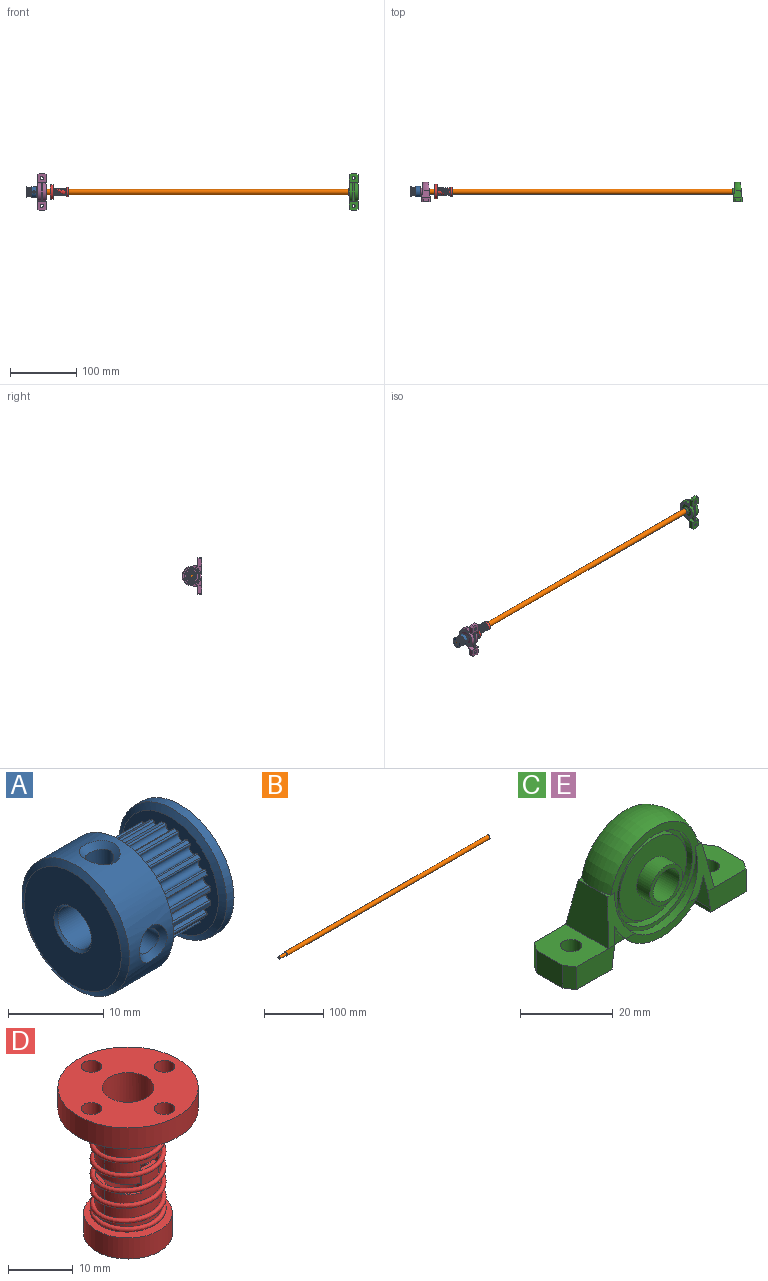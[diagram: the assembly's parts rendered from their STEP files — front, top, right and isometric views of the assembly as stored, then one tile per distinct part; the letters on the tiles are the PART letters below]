
ASSEMBLY  parts=5 mates=5
PART A: 99 faces, bbox 16x16.1x16.3 mm
  f0: plane 16.3x16.15mm, normal (1,0,0), area 136.4mm2, adj f1,f2
  f1: cylinder r=8mm len=16mm, axis (-1,0,0), area 55.3mm2, adj f0,f3
  f2: cone r=4.38mm half-angle=45deg, axis (1,0,0), area 6mm2, adj f0,f4
  f3: cone r=7.21mm half-angle=60.2deg, axis (1,0,0), area 43.3mm2, adj f1,f5
  f4: cone r=4.23mm half-angle=45deg, axis (-1,0,0), area 5.8mm2, adj f2,f6
  f5: plane 14.69x14.43mm, normal (-1,0,0), area 61.1mm2, adj f3,f7,f8,f9,f10,f11,f12,f13
  f6: plane 8.62x8.54mm, normal (1,0,0), area 31.6mm2, adj f4,f87
  f7: cylinder r=0.55mm len=7mm, axis (-1,0,0), area 12.5mm2, adj f5,f8,f86,f90
  f8: cylinder r=0.16mm len=7mm, axis (-1,0,0), area 2mm2, adj f5,f7,f9,f90
  f9: cylinder r=6.11mm len=7mm, axis (-1,0,0), area 3.2mm2, adj f5,f8,f10,f90
  f10: cylinder r=0.16mm len=7mm, axis (1,0,0), area 2mm2, adj f5,f9,f11,f90
  f11: cylinder r=0.55mm len=7mm, axis (-1,0,0), area 12.5mm2, adj f5,f10,f12,f90
  f12: cylinder r=0.16mm len=7mm, axis (-1,0,0), area 2mm2, adj f5,f11,f13,f90
  f13: cylinder r=6.11mm len=7mm, axis (-1,0,0), area 3.2mm2, adj f5,f12,f14,f90
  f14: cylinder r=0.16mm len=7mm, axis (1,0,0), area 2mm2, adj f5,f13,f15,f90
  f15: cylinder r=0.55mm len=7mm, axis (-1,0,0), area 12.5mm2, adj f5,f14,f16,f90
  f16: cylinder r=0.16mm len=7mm, axis (-1,0,0), area 2mm2, adj f5,f15,f17,f90
  f17: cylinder r=6.11mm len=7mm, axis (-1,0,0), area 3.2mm2, adj f5,f16,f18,f90
  f18: cylinder r=0.16mm len=7mm, axis (1,0,0), area 2mm2, adj f5,f17,f19,f90
  f19: cylinder r=0.55mm len=7mm, axis (-1,0,0), area 12.5mm2, adj f5,f18,f20,f90
  f20: cylinder r=0.16mm len=7mm, axis (-1,0,0), area 2mm2, adj f5,f19,f21,f90
  f21: cylinder r=6.11mm len=7mm, axis (-1,0,0), area 3.2mm2, adj f5,f20,f22,f90
  f22: cylinder r=0.16mm len=7mm, axis (1,0,0), area 2mm2, adj f5,f21,f23,f90
  f23: cylinder r=0.55mm len=7mm, axis (-1,0,0), area 12.5mm2, adj f5,f22,f24,f90
  f24: cylinder r=0.16mm len=7mm, axis (-1,0,0), area 2mm2, adj f5,f23,f25,f90
  f25: cylinder r=6.11mm len=7mm, axis (-1,0,0), area 3.2mm2, adj f5,f24,f26,f90
  f26: cylinder r=0.16mm len=7mm, axis (1,0,0), area 2mm2, adj f5,f25,f27,f90
  f27: cylinder r=0.55mm len=7mm, axis (-1,0,0), area 12.5mm2, adj f5,f26,f28,f90
  f28: cylinder r=0.16mm len=7mm, axis (-1,0,0), area 2mm2, adj f5,f27,f29,f90
  f29: cylinder r=6.11mm len=7mm, axis (-1,0,0), area 3.2mm2, adj f5,f28,f30,f90
  f30: cylinder r=0.16mm len=7mm, axis (1,0,0), area 2mm2, adj f5,f29,f31,f90
  f31: cylinder r=0.55mm len=7mm, axis (-1,0,0), area 12.5mm2, adj f5,f30,f32,f90
  f32: cylinder r=0.16mm len=7mm, axis (-1,0,0), area 2mm2, adj f5,f31,f33,f90
  f33: cylinder r=6.11mm len=7mm, axis (-1,0,0), area 3.2mm2, adj f5,f32,f34,f90
  f34: cylinder r=0.16mm len=7mm, axis (1,0,0), area 2mm2, adj f5,f33,f35,f90
  f35: cylinder r=0.55mm len=7mm, axis (-1,0,0), area 12.5mm2, adj f5,f34,f36,f90
  f36: cylinder r=0.16mm len=7mm, axis (-1,0,0), area 2mm2, adj f5,f35,f37,f90
  f37: cylinder r=6.11mm len=7mm, axis (-1,0,0), area 3.2mm2, adj f5,f36,f38,f90
  f38: cylinder r=0.16mm len=7mm, axis (1,0,0), area 2mm2, adj f5,f37,f39,f90
  f39: cylinder r=0.55mm len=7mm, axis (-1,0,0), area 12.5mm2, adj f5,f38,f40,f90
  f40: cylinder r=0.16mm len=7mm, axis (-1,0,0), area 2mm2, adj f5,f39,f41,f90
  f41: cylinder r=6.11mm len=7mm, axis (-1,0,0), area 3.2mm2, adj f5,f40,f42,f90
  f42: cylinder r=0.16mm len=7mm, axis (1,0,0), area 2mm2, adj f5,f41,f43,f90
  f43: cylinder r=0.55mm len=7mm, axis (-1,0,0), area 12.5mm2, adj f5,f42,f44,f90
  f44: cylinder r=0.16mm len=7mm, axis (-1,0,0), area 2mm2, adj f5,f43,f45,f90
  f45: cylinder r=6.11mm len=7mm, axis (-1,0,0), area 3.2mm2, adj f5,f44,f46,f90
  f46: cylinder r=0.16mm len=7mm, axis (1,0,0), area 2mm2, adj f5,f45,f47,f90
  f47: cylinder r=0.55mm len=7mm, axis (-1,0,0), area 12.5mm2, adj f5,f46,f48,f90
  f48: cylinder r=0.16mm len=7mm, axis (-1,0,0), area 2mm2, adj f5,f47,f49,f90
  f49: cylinder r=6.11mm len=7mm, axis (-1,0,0), area 3.2mm2, adj f5,f48,f50,f90
  f50: cylinder r=0.16mm len=7mm, axis (1,0,0), area 2mm2, adj f5,f49,f51,f90
  f51: cylinder r=0.55mm len=7mm, axis (-1,0,0), area 12.5mm2, adj f5,f50,f52,f90
  f52: cylinder r=0.16mm len=7mm, axis (-1,0,0), area 2mm2, adj f5,f51,f53,f90
  f53: cylinder r=6.11mm len=7mm, axis (-1,0,0), area 3.2mm2, adj f5,f52,f54,f90
  f54: cylinder r=0.16mm len=7mm, axis (1,0,0), area 2mm2, adj f5,f53,f55,f90
  f55: cylinder r=0.55mm len=7mm, axis (-1,0,0), area 12.5mm2, adj f5,f54,f56,f90
  f56: cylinder r=0.16mm len=7mm, axis (-1,0,0), area 2mm2, adj f5,f55,f57,f90
  f57: cylinder r=6.11mm len=7mm, axis (-1,0,0), area 3.2mm2, adj f5,f56,f58,f90
  f58: cylinder r=0.16mm len=7mm, axis (1,0,0), area 2mm2, adj f5,f57,f59,f90
  f59: cylinder r=0.55mm len=7mm, axis (-1,0,0), area 12.5mm2, adj f5,f58,f60,f90
  f60: cylinder r=0.16mm len=7mm, axis (-1,0,0), area 2mm2, adj f5,f59,f61,f90
  f61: cylinder r=6.11mm len=7mm, axis (-1,0,0), area 3.2mm2, adj f5,f60,f62,f90
  f62: cylinder r=0.16mm len=7mm, axis (1,0,0), area 2mm2, adj f5,f61,f63,f90
  f63: cylinder r=0.55mm len=7mm, axis (-1,0,0), area 12.5mm2, adj f5,f62,f64,f90
  f64: cylinder r=0.16mm len=7mm, axis (-1,0,0), area 2mm2, adj f5,f63,f65,f90
  f65: cylinder r=6.11mm len=7mm, axis (-1,0,0), area 3.2mm2, adj f5,f64,f66,f90
  f66: cylinder r=0.16mm len=7mm, axis (1,0,0), area 2mm2, adj f5,f65,f67,f90
  f67: cylinder r=0.55mm len=7mm, axis (-1,0,0), area 12.5mm2, adj f5,f66,f68,f90
  f68: cylinder r=0.16mm len=7mm, axis (-1,0,0), area 2mm2, adj f5,f67,f69,f90
  f69: cylinder r=6.11mm len=7mm, axis (-1,0,0), area 3.2mm2, adj f5,f68,f70,f90
  f70: cylinder r=0.16mm len=7mm, axis (1,0,0), area 2mm2, adj f5,f69,f71,f90
  f71: cylinder r=0.55mm len=7mm, axis (-1,0,0), area 12.5mm2, adj f5,f70,f72,f90
  f72: cylinder r=0.16mm len=7mm, axis (-1,0,0), area 2mm2, adj f5,f71,f73,f90
  f73: cylinder r=6.11mm len=7mm, axis (-1,0,0), area 3.2mm2, adj f5,f72,f74,f90
  f74: cylinder r=0.16mm len=7mm, axis (1,0,0), area 2mm2, adj f5,f73,f75,f90
  f75: cylinder r=0.55mm len=7mm, axis (-1,0,0), area 12.5mm2, adj f5,f74,f76,f90
  f76: cylinder r=0.16mm len=7mm, axis (-1,0,0), area 2mm2, adj f5,f75,f77,f90
  f77: cylinder r=6.11mm len=7mm, axis (-1,0,0), area 3.2mm2, adj f5,f76,f78,f90
  f78: cylinder r=0.16mm len=7mm, axis (1,0,0), area 2mm2, adj f5,f77,f79,f90
  f79: cylinder r=0.55mm len=7mm, axis (-1,0,0), area 12.5mm2, adj f5,f78,f80,f90
  f80: cylinder r=0.16mm len=7mm, axis (-1,0,0), area 2mm2, adj f5,f79,f81,f90
  f81: cylinder r=6.11mm len=7mm, axis (-1,0,0), area 3.2mm2, adj f5,f80,f82,f90
  f82: cylinder r=0.16mm len=7mm, axis (1,0,0), area 2mm2, adj f5,f81,f83,f90
  f83: cylinder r=0.55mm len=7mm, axis (-1,0,0), area 12.5mm2, adj f5,f82,f84,f90
  f84: cylinder r=0.16mm len=7mm, axis (-1,0,0), area 2mm2, adj f5,f83,f85,f90
  f85: cylinder r=6.11mm len=7mm, axis (-1,0,0), area 3.2mm2, adj f5,f84,f86,f90
  f86: cylinder r=0.16mm len=7mm, axis (1,0,0), area 2mm2, adj f5,f7,f85,f90
  f87: cone r=2.5mm half-angle=45deg, axis (1,0,0), area 7.1mm2, adj f6,f92
  f88: cone r=2.8mm half-angle=45deg, axis (-1,0,0), area 7.1mm2, adj f91,f92
  f89: cylinder r=1.5mm len=4.84mm, axis (0,1,0), area 45.6mm2, adj f92,f93
  f90: plane 14.69x14.56mm, normal (1,0,0), area 61.1mm2, adj f7,f8,f9,f10,f11,f12,f13,f14
  f91: plane 14.69x14.43mm, normal (-1,0,0), area 138.8mm2, adj f88,f95
  f92: cylinder r=2.5mm len=15.4mm, axis (1,0,0), area 227mm2, adj f87,f88,f89,f96
  f93: bspline ~4.49x4.12mm, area 10.7mm2, adj f89,f97
  f94: cone r=8mm half-angle=60.2deg, axis (-1,0,0), area 43.3mm2, adj f90,f97
  f95: cone r=7.21mm half-angle=60.2deg, axis (1,0,0), area 43.3mm2, adj f91,f97
  f96: cylinder r=1.5mm len=4.84mm, axis (0,0,-1), area 45.6mm2, adj f92,f98
  f97: cylinder r=8mm len=16mm, axis (-1,0,0), area 299.7mm2, adj f93,f94,f95,f98
  f98: bspline ~4.49x4.12mm, area 10.7mm2, adj f96,f97
PART B: 5 faces, bbox 500x8x8 mm
  f0: plane 8x8mm, normal (1,0,0), area 50.3mm2, adj f1
  f1: cylinder r=4mm len=484mm, axis (-1,0,0), area 12164.2mm2, adj f0,f2
  f2: plane 8x8mm, normal (-1,0,0), area 30.6mm2, adj f1,f3
  f3: cylinder r=2.5mm len=16mm, axis (-1,0,0), area 251.3mm2, adj f2,f4
  f4: plane 5x5mm, normal (-1,0,0), area 19.6mm2, adj f3
PART C: 59 faces, bbox 55x14.5x29 mm
  f0: plane 23x23mm, normal (0,1,0), area 85.4mm2, adj f22,f51
  f1: plane 23x23mm, normal (0,-1,0), area 85.4mm2, adj f23,f50
  f2: cylinder r=14.5mm len=27.02mm, axis (0,1,0), area 177.4mm2, adj f3,f4,f17,f43,f44,f46,f47
  f3: plane 9.24x5.2mm, normal (0.99,0,-0.16), area 47.1mm2, adj f2,f18,f37,f44,f46
  f4: plane 9.24x5.2mm, normal (-0.99,0,-0.16), area 47.1mm2, adj f2,f16,f40,f43,f47
  f5: plane 4.5x1.02mm, normal (0,0,1), area 1.5mm2, adj f7,f19,f47
  f6: plane 4.5x1.02mm, normal (0,0,1), area 1.5mm2, adj f8,f19,f46
  f7: plane 13x11.79mm, normal (0.99,0,0.16), area 131.3mm2, adj f5,f24,f33,f47,f48
  f8: plane 13x11.79mm, normal (-0.99,0,0.16), area 131.3mm2, adj f6,f25,f39,f46,f49
  f9: cylinder r=14.5mm len=27.02mm, axis (0,1,0), area 177.4mm2, adj f11,f12,f14,f42,f45,f48,f49
  f10: cylinder r=12.5mm len=25mm, axis (0,1,0), area 63.2mm2, adj f14,f20,f48,f49
  f11: plane 9.24x5.2mm, normal (0.99,0,-0.16), area 47.1mm2, adj f9,f15,f37,f45,f49
  f12: plane 9.24x5.2mm, normal (-0.99,0,-0.16), area 47.1mm2, adj f9,f13,f40,f42,f48
  f13: plane 11.65x6mm, normal (0,1,0), area 67.1mm2, adj f12,f27,f32,f33,f40,f48
  f14: plane 21.91x5mm, normal (0,1,0), area 42.6mm2, adj f9,f10,f48,f49
  f15: plane 11.65x6mm, normal (0,1,0), area 67.1mm2, adj f11,f31,f36,f37,f39,f49
  f16: plane 11.65x6mm, normal (0,-1,0), area 67.1mm2, adj f4,f29,f32,f33,f40,f47
  f17: plane 21.91x5mm, normal (0,-1,0), area 42.6mm2, adj f2,f26,f46,f47
  f18: plane 11.65x6mm, normal (0,-1,0), area 67.1mm2, adj f3,f31,f34,f37,f39,f46
  f19: torus R=3.88mm, axis (0,1,0), area 370.9mm2, adj f5,f6,f20,f21,f24,f25
  f20: plane 26.61x26mm, normal (0,1,0), area 111.6mm2, adj f10,f19,f22,f48,f49
  f21: plane 26.61x26mm, normal (0,-1,0), area 111.6mm2, adj f19,f23,f26,f46,f47
  f22: cylinder r=11.5mm len=23mm, axis (0,1,0), area 144.5mm2, adj f0,f20
  f23: cylinder r=11.5mm len=23mm, axis (0,1,0), area 144.5mm2, adj f1,f21
  f24: plane 4.5x1.02mm, normal (0,0,1), area 1.5mm2, adj f7,f19,f48
  f25: plane 4.5x1.02mm, normal (0,0,1), area 1.5mm2, adj f8,f19,f49
  f26: cylinder r=12.5mm len=25mm, axis (0,1,0), area 63.2mm2, adj f17,f21,f46,f47
  f27: plane 6x2.5mm, normal (0.83,0.55,0), area 18mm2, adj f13,f28,f32,f33
  f28: plane 8x6mm, normal (1,0,0), area 48mm2, adj f27,f29,f32,f33
  f29: plane 6x2.5mm, normal (0.83,-0.55,0), area 18mm2, adj f16,f28,f32,f33
  f30: cylinder r=2.3mm len=6mm, axis (0,0,-1), area 86.7mm2, adj f32,f33
  f31: plane 13x12.5mm, normal (0,0,-1), area 141.7mm2, adj f15,f18,f34,f35,f36,f37,f38
  f32: plane 13x12.5mm, normal (0,0,-1), area 141.7mm2, adj f13,f16,f27,f28,f29,f30,f40
  f33: plane 13x11.3mm, normal (0,0,1), area 126.1mm2, adj f7,f13,f16,f27,f28,f29,f30
  f34: plane 6x2.5mm, normal (-0.83,-0.55,0), area 18mm2, adj f18,f31,f35,f39
  f35: plane 8x6mm, normal (-1,0,0), area 48mm2, adj f31,f34,f36,f39
  f36: plane 6x2.5mm, normal (-0.83,0.55,0), area 18mm2, adj f15,f31,f35,f39
  f37: plane 13x1mm, normal (1,0,0), area 13mm2, adj f3,f11,f15,f18,f31,f41
  f38: cylinder r=2.3mm len=6mm, axis (0,0,-1), area 86.7mm2, adj f31,f39
  f39: plane 13x11.3mm, normal (0,0,1), area 126.1mm2, adj f8,f15,f18,f34,f35,f36,f38
  f40: plane 13x1mm, normal (-1,0,0), area 13mm2, adj f4,f12,f13,f16,f32,f41
  f41: plane 30x2.6mm, normal (0,0,-1), area 78mm2, adj f37,f40,f42,f43,f44,f45
  f42: plane 15x9.24mm, normal (0,1,0), area 41.1mm2, adj f9,f12,f41
  f43: plane 15x9.24mm, normal (0,-1,0), area 41.1mm2, adj f2,f4,f41
  f44: plane 15x9.24mm, normal (0,-1,0), area 41.1mm2, adj f2,f3,f41
  f45: plane 15x9.24mm, normal (0,1,0), area 41.1mm2, adj f9,f11,f41
  f46: plane 11.79x8.08mm, normal (0,-0.99,0.17), area 39.8mm2, adj f2,f3,f6,f8,f17,f18,f21,f26
  f47: plane 11.79x8.08mm, normal (0,-0.99,0.17), area 39.8mm2, adj f2,f4,f5,f7,f16,f17,f21,f26
  f48: plane 11.79x8.08mm, normal (0,0.99,0.17), area 39.8mm2, adj f7,f9,f10,f12,f13,f14,f20,f24
  f49: plane 11.79x8.08mm, normal (0,0.99,0.17), area 39.8mm2, adj f8,f9,f10,f11,f14,f15,f20,f25
  f50: cylinder r=10.25mm len=20.5mm, axis (0,1,0), area 96.6mm2, adj f1,f52
  f51: cylinder r=10.25mm len=20.5mm, axis (0,1,0), area 96.6mm2, adj f0,f53
  f52: plane 20.5x20.5mm, normal (0,-1,0), area 251.5mm2, adj f50,f54
  f53: plane 20.5x20.5mm, normal (0,1,0), area 251.5mm2, adj f51,f56
  f54: cylinder r=5mm len=10mm, axis (0,1,0), area 125.7mm2, adj f52,f57
  f55: cylinder r=4mm len=13mm, axis (0,1,0), area 326.7mm2, adj f57,f58
  f56: cylinder r=5mm len=10mm, axis (0,1,0), area 31.4mm2, adj f53,f58
  f57: plane 10x10mm, normal (0,-1,0), area 28.3mm2, adj f54,f55
  f58: plane 10x10mm, normal (0,1,0), area 28.3mm2, adj f55,f56
PART D: 46 faces, bbox 21.8x21.8x27.8 mm
  f0: plane 13.75x13.75mm, normal (0,0,1), area 63.5mm2, adj f9,f34,f36,f43
  f1: plane 4.04x1.3mm, normal (1,0,0), area 5mm2, adj f2,f10,f14,f15,f38,f45
  f2: bspline ~18x11.79mm, area 444.7mm2, adj f1,f3,f9,f10,f11,f12,f14,f16
  f3: plane 3.56x1.35mm, normal (-1,0,0), area 4.5mm2, adj f2,f18,f19,f27,f28,f31
  f4: cylinder r=10.88mm len=21.75mm, axis (0,0,-1), area 273.3mm2, adj f5,f20
  f5: plane 21.77x21.77mm, normal (0,0,-1), area 255.4mm2, adj f4,f6,f7,f21,f22,f23,f37,f42
  f6: cylinder r=1.6mm len=4mm, axis (0,0,-1), area 40.2mm2, adj f5,f20
  f7: cylinder r=1.6mm len=4mm, axis (0,0,-1), area 40.2mm2, adj f5,f20
  f8: plane 9.58x3.22mm, normal (0,0,-1), area 12.1mm2, adj f17,f28,f29,f33
  f9: cylinder r=5.15mm len=10.3mm, axis (0,0,-1), area 24.4mm2, adj f0,f2,f12,f34,f36
  f10: cylinder r=5.15mm len=10.3mm, axis (0,0,-1), area 37.1mm2, adj f1,f2,f11,f16,f39,f40,f41,f45
  f11: cylinder r=5.15mm len=10.3mm, axis (0,0,-1), area 79.1mm2, adj f2,f10,f12,f40
  f12: cylinder r=5.15mm len=10.3mm, axis (0,0,-1), area 62.3mm2, adj f2,f9,f11,f36
  f13: plane 3.75x1.62mm, normal (0,0,1), area 4.4mm2, adj f15,f16,f35,f39
  f14: plane 3.75x1.62mm, normal (0,0,1), area 4.4mm2, adj f1,f2,f15,f38,f41
  f15: cylinder r=4mm len=15mm, axis (0,0,-1), area 307.7mm2, adj f1,f13,f14,f16,f39,f40,f41,f44
  f16: plane 4.04x1.3mm, normal (1,0,0), area 5mm2, adj f2,f10,f13,f15,f35,f45
  f17: cylinder r=5.17mm len=9.58mm, axis (0,0,1), area 17mm2, adj f2,f8,f29,f33
  f18: cylinder r=5.17mm len=4.32mm, axis (0,0,1), area 1.4mm2, adj f2,f3,f27
  f19: cylinder r=5.17mm len=9.58mm, axis (0,0,1), area 29.5mm2, adj f2,f3,f27,f30
  f20: plane 21.75x21.75mm, normal (0,0,1), area 289.1mm2, adj f4,f6,f7,f21,f22,f28
  f21: cylinder r=1.6mm len=4mm, axis (0,0,-1), area 40.2mm2, adj f5,f20
  f22: cylinder r=1.6mm len=4mm, axis (0,0,-1), area 40.2mm2, adj f5,f20
  f23: cylinder r=5.17mm len=10.34mm, axis (0,0,1), area 49.1mm2, adj f2,f5,f26,f37,f42
  f24: cylinder r=5.17mm len=5.63mm, axis (0,0,1), area 15mm2, adj f2,f25,f29,f31
  f25: cylinder r=5.17mm len=10.34mm, axis (0,0,1), area 74.7mm2, adj f2,f24,f26,f30,f32,f33
  f26: cylinder r=5.17mm len=10.34mm, axis (0,0,1), area 75.9mm2, adj f2,f23,f25,f42
  f27: plane 9.59x3.23mm, normal (0,0,-1), area 11.9mm2, adj f2,f3,f18,f19,f28,f30
  f28: cylinder r=4mm len=14.8mm, axis (0,0,-1), area 343.4mm2, adj f3,f8,f20,f27,f29,f30,f31,f32
  f29: plane 3.56x1.35mm, normal (1,0,0), area 4.5mm2, adj f2,f8,f17,f24,f28,f31
  f30: plane 3.56x1.35mm, normal (-1,0,0), area 4.5mm2, adj f2,f19,f25,f27,f28,f32
  f31: plane 3.91x1.69mm, normal (0,0,-1), area 4.7mm2, adj f2,f3,f24,f28,f29
  f32: plane 3.9x1.68mm, normal (0,0,-1), area 4.7mm2, adj f25,f28,f30,f33
  f33: plane 3.56x1.35mm, normal (1,0,0), area 4.5mm2, adj f2,f8,f17,f25,f28,f32
  f34: plane 0.78x0.74mm, normal (1,0,0), area 0.5mm2, adj f0,f9,f36
  f35: cylinder r=5.15mm len=3.75mm, axis (0,0,-1), area 3.9mm2, adj f2,f13,f16,f39
  f36: bspline ~11.79x11.79mm, area 72.7mm2, adj f0,f2,f9,f12,f34
  f37: plane 0.82x0.74mm, normal (-1,0,0), area 0.5mm2, adj f5,f23,f42
  f38: cylinder r=5.15mm len=3.75mm, axis (0,0,-1), area 9.3mm2, adj f1,f2,f14,f41
  f39: plane 4.04x1.3mm, normal (-1,0,0), area 5mm2, adj f2,f10,f13,f15,f35,f40
  f40: plane 9.56x3.28mm, normal (0,0,1), area 12.1mm2, adj f2,f10,f11,f15,f39,f41
  f41: plane 4.04x1.3mm, normal (-1,0,0), area 5mm2, adj f2,f10,f14,f15,f38,f40
  f42: bspline ~11.79x11.79mm, area 71.5mm2, adj f2,f5,f23,f26,f37
  f43: cylinder r=6.88mm len=13.75mm, axis (0,0,-1), area 172.8mm2, adj f0,f44
  f44: plane 13.75x13.75mm, normal (0,0,-1), area 98.2mm2, adj f15,f43
  f45: plane 9.59x3.28mm, normal (0,0,1), area 12.1mm2, adj f1,f10,f15,f16
PART E: same geometry as C
PLACE A rot(axis=(0,-1,0),180deg) t=(-344.72,0.3,45.5)mm
PLACE B rot(axis=(1,0,0),0deg) t=(-360.72,0.3,45.5)mm
PLACE C rot(axis=(-0.58,-0.58,-0.58),120deg) t=(132.78,0.3,45.5)mm
PLACE D rot(axis=(0,-1,0),90deg) t=(-256.22,0.3,45.5)mm
PLACE E rot(axis=(-0.58,-0.58,-0.58),120deg) t=(-338.22,0.3,45.5)mm fixed
MATE fastened A.f1 <-> B.f1  axis (1,0,0) through (-344.72,0.3,45.5)mm
MATE slider D.f4 <-> C.f19  axis (-1,0,0) through (-323.72,0.3,45.5)mm
MATE fastened E.f19 <-> B.f1  axis (-1,0,0) through (-344.72,0.3,45.5)mm
MATE parallel E.f32 <-> C.f32  axis (0,-1,0) through (-336.72,-15.2,60.5)mm
MATE fastened C.f19 <-> B.f1  axis (1,0,0) through (139.28,0.3,45.5)mm
